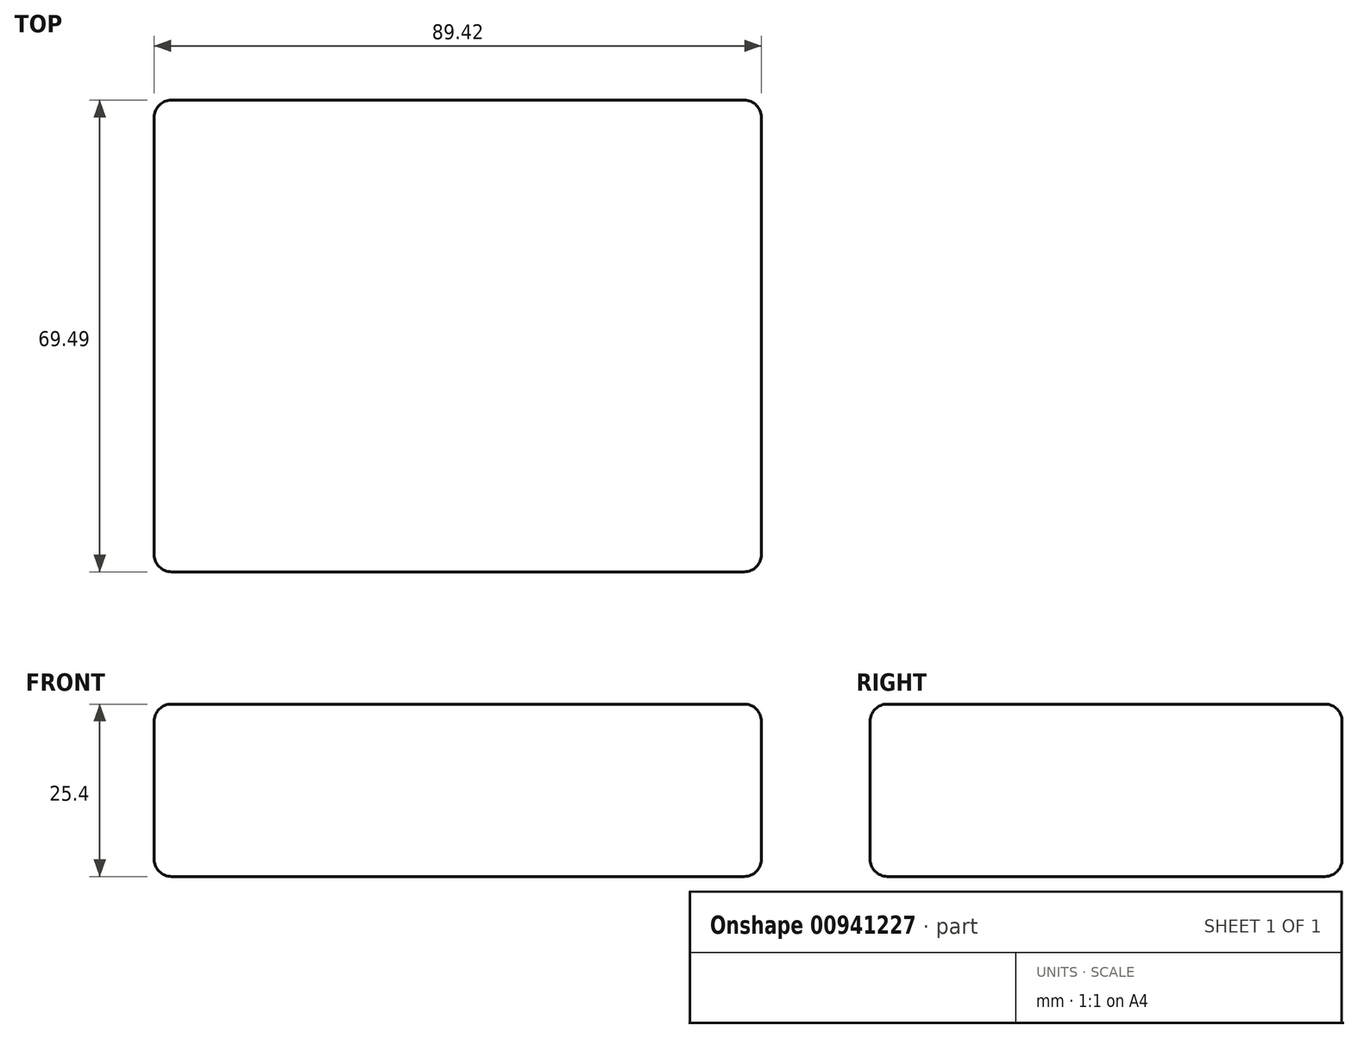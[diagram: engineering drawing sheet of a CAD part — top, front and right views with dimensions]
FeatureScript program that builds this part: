
annotation { "Feature Type Name" : "Feature", "Feature Type Description" : "" }
export const myFeature = defineFeature(function(context is Context, id is Id, definition is map)
    precondition{}
    {
        {
            var Q0;
            Q0=qCreatedBy(makeId("Top.planeOp"),FACE);
            var sketch = newSketch(context, id + "F0", { "sketchPlane" : qUnion([Q0])});
            skLineSegment(sketch, "E0.bottom", {"start": v(-42.42, -41.84) * mm, "end": v(47, -41.84) * mm});
            skLineSegment(sketch, "E0.top", {"start": v(-42.42, 27.65) * mm, "end": v(47, 27.65) * mm});
            skLineSegment(sketch, "E0.left", {"start": v(-42.42, -41.84) * mm, "end": v(-42.42, 27.65) * mm});
            skLineSegment(sketch, "E0.right", {"start": v(47, -41.84) * mm, "end": v(47, 27.65) * mm});
            skSolve(sketch);
        }
        {
            var Q0;
            Q0 = qSketchRegion(id + "F0", true);
            extrude(context, id + "F1", {"entities" : qUnion([Q0]), "depth" : 25.4 * mm, "offsetDistance" : 25.4 * mm});
        }
        {
            var Q0;
            Q0=makeQuery(id+"F1.opExtrude","CAP_EDGE",EDGE,{"disambiguationData":[OSD([sQuery(id+"F0.wireOp",EDGE,"E0.bottom")])],"isStart":false});
            var Q1;
            Q1=makeQuery(id+"F1.opExtrude","CAP_EDGE",EDGE,{"disambiguationData":[OSD([sQuery(id+"F0.wireOp",EDGE,"E0.right")])],"isStart":false});
            var Q2;
            Q2=makeQuery(id+"F1.opExtrude","CAP_EDGE",EDGE,{"disambiguationData":[OSD([sQuery(id+"F0.wireOp",EDGE,"E0.top")])],"isStart":false});
            var Q3;
            Q3=makeQuery(id+"F1.opExtrude","CAP_EDGE",EDGE,{"disambiguationData":[OSD([sQuery(id+"F0.wireOp",EDGE,"E0.left")])],"isStart":false});
            var Q4;
            Q4=makeQuery(id+"F1.opExtrude","SWEPT_EDGE",EDGE,{"disambiguationData":[OSD([sQuery(id+"F0.wireOp",EDGE,"E0.bottom"),sQuery(id+"F0.wireOp",EDGE,"E0.right")])]});
            var Q5;
            Q5=makeQuery(id+"F1.opExtrude","CAP_EDGE",EDGE,{"disambiguationData":[OSD([sQuery(id+"F0.wireOp",EDGE,"E0.bottom")])],"isStart":true});
            var Q6;
            Q6=makeQuery(id+"F1.opExtrude","CAP_EDGE",EDGE,{"disambiguationData":[OSD([sQuery(id+"F0.wireOp",EDGE,"E0.right")])],"isStart":true});
            var Q7;
            Q7=makeQuery(id+"F1.opExtrude","SWEPT_EDGE",EDGE,{"disambiguationData":[OSD([sQuery(id+"F0.wireOp",EDGE,"E0.top"),sQuery(id+"F0.wireOp",EDGE,"E0.right")])]});
            var Q8;
            Q8=makeQuery(id+"F1.opExtrude","CAP_EDGE",EDGE,{"disambiguationData":[OSD([sQuery(id+"F0.wireOp",EDGE,"E0.top")])],"isStart":true});
            var Q9;
            Q9=makeQuery(id+"F1.opExtrude","SWEPT_EDGE",EDGE,{"disambiguationData":[OSD([sQuery(id+"F0.wireOp",EDGE,"E0.top"),sQuery(id+"F0.wireOp",EDGE,"E0.left")])]});
            var Q10;
            Q10=makeQuery(id+"F1.opExtrude","CAP_EDGE",EDGE,{"disambiguationData":[OSD([sQuery(id+"F0.wireOp",EDGE,"E0.left")])],"isStart":true});
            var Q11;
            Q11=makeQuery(id+"F1.opExtrude","SWEPT_EDGE",EDGE,{"disambiguationData":[OSD([sQuery(id+"F0.wireOp",EDGE,"E0.bottom"),sQuery(id+"F0.wireOp",EDGE,"E0.left")])]});
            fillet(context, id + "F2", {"entities" : qUnion([Q0, Q1, Q2, Q3, Q4, Q5, Q6, Q7, Q8, Q9, Q10, Q11]), "radius" : 2.54 * mm, "tangentPropagation" : true, "allowEdgeOverflow" : false});
        }
    });
